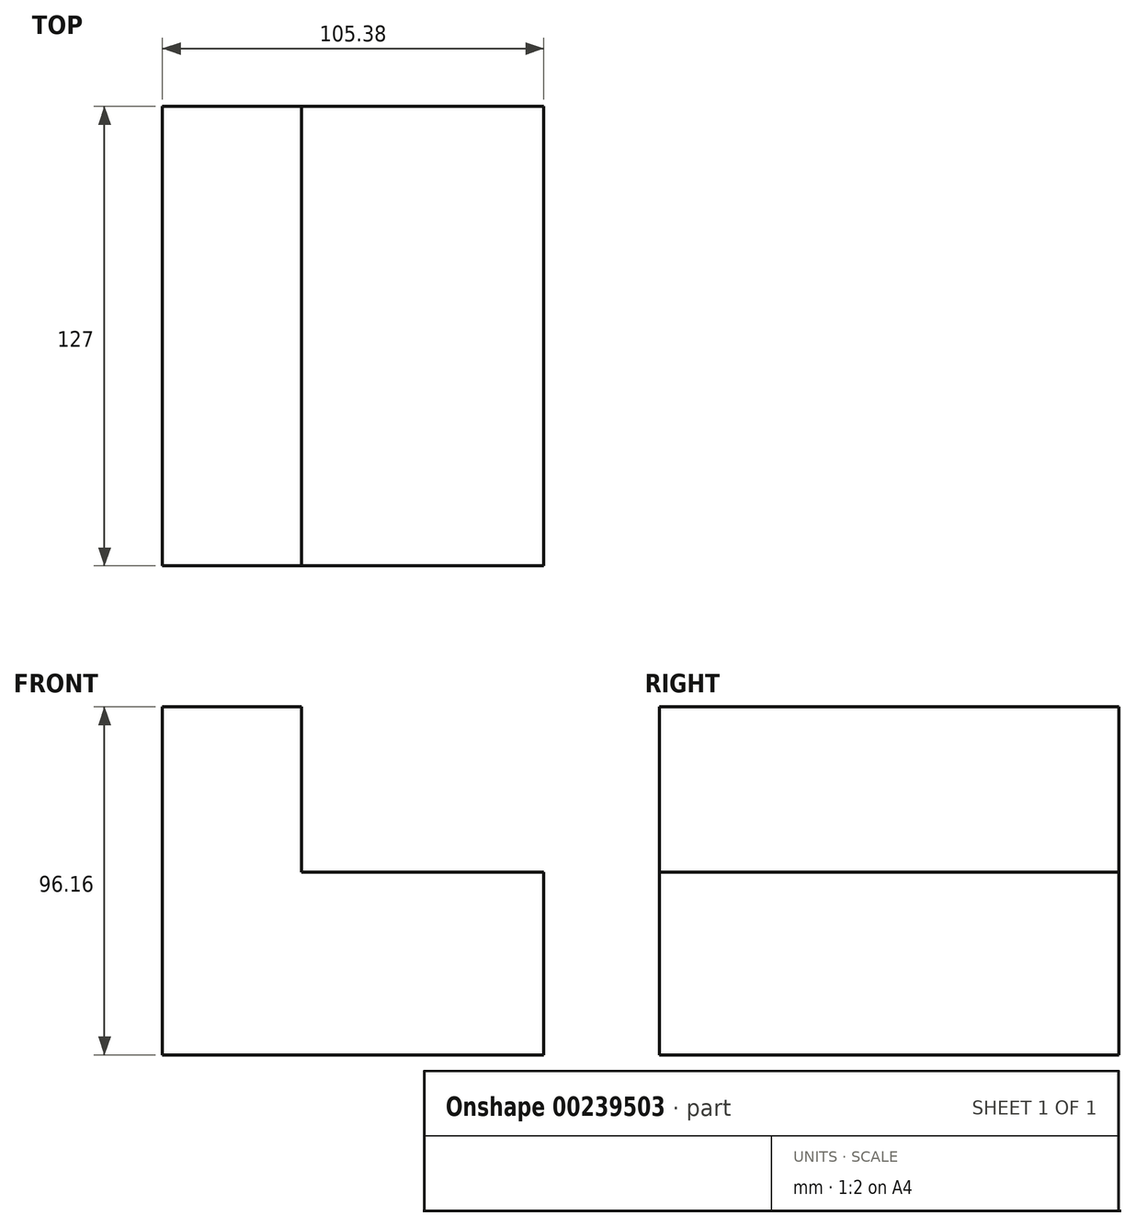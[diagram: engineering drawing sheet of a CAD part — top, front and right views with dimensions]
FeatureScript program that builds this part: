
annotation { "Feature Type Name" : "Feature", "Feature Type Description" : "" }
export const myFeature = defineFeature(function(context is Context, id is Id, definition is map)
    precondition{}
    {
        {
            var Q0;
            Q0=qCreatedBy(makeId("Front.planeOp"),FACE);
            var sketch = newSketch(context, id + "F0", { "sketchPlane" : qUnion([Q0])});
            skLineSegment(sketch, "E0.bottom", {"start": v(52.7, 48.08) * mm, "end": v(-52.7, 48.08) * mm});
            skLineSegment(sketch, "E0.top", {"start": v(52.7, -48.08) * mm, "end": v(-52.7, -48.08) * mm});
            skLineSegment(sketch, "E0.left", {"start": v(52.7, 48.08) * mm, "end": v(52.7, -48.08) * mm});
            skLineSegment(sketch, "E0.right", {"start": v(-52.7, 48.08) * mm, "end": v(-52.7, -48.08) * mm});
            skPoint(sketch, "E0.middle", {"position": v(0, 0) * mm});
            skSolve(sketch);
        }
        {
            var Q0;
            Q0 = qSketchRegion(id + "F0", true);
            extrude(context, id + "F1", {"entities" : qUnion([Q0]), "depth" : 127 * mm});
        }
        {
            var Q0;
            Q0=makeQuery(id+"F1.opExtrude","CAP_FACE",FACE,{"disambiguationData":[OSD([sQuery(id+"F0.wireOp",EDGE,"E0.bottom"),sQuery(id+"F0.wireOp",EDGE,"E0.top"),sQuery(id+"F0.wireOp",EDGE,"E0.left"),sQuery(id+"F0.wireOp",EDGE,"E0.right")])],"isStart":false});
            var sketch = newSketch(context, id + "F2", { "sketchPlane" : qUnion([Q0])});
            skLineSegment(sketch, "E1.bottom", {"start": v(-14.3, 48.08) * mm, "end": v(52.7, 48.08) * mm});
            skLineSegment(sketch, "E1.top", {"start": v(-14.3, 2.45) * mm, "end": v(52.7, 2.45) * mm});
            skLineSegment(sketch, "E1.left", {"start": v(-14.3, 48.08) * mm, "end": v(-14.3, 2.45) * mm});
            skLineSegment(sketch, "E1.right", {"start": v(52.7, 48.08) * mm, "end": v(52.7, 2.45) * mm});
            skSolve(sketch);
        }
        {
            var Q0;
            Q0 = qSketchRegion(id + "F2", true);
            extrude(context, id + "F3", {"entities" : qUnion([Q0]), "operationType" : NewBodyOperationType.REMOVE, "endBound" : BoundingType.SYMMETRIC, "oppositeDirection" : true, "depth" : 310.4 * mm});
        }
    });
